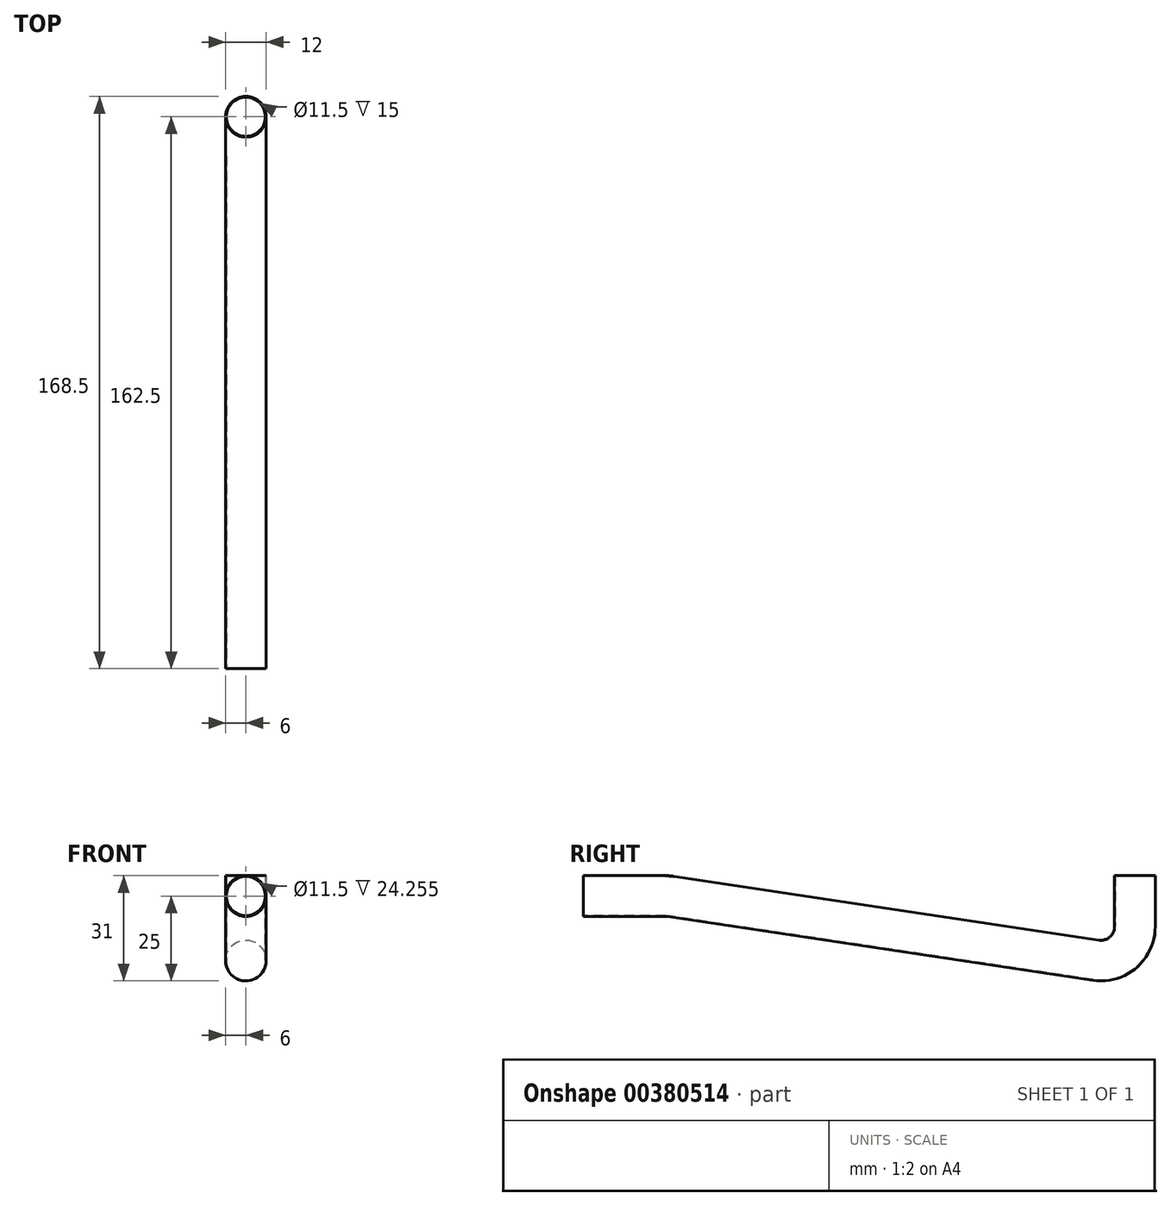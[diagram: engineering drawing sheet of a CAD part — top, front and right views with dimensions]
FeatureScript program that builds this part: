
annotation { "Feature Type Name" : "Feature", "Feature Type Description" : "" }
export const myFeature = defineFeature(function(context is Context, id is Id, definition is map)
    precondition{}
    {
        {
            var Q0;
            Q0=qCreatedBy(makeId("Right.planeOp"),FACE);
            var sketch = newSketch(context, id + "F0", { "sketchPlane" : qUnion([Q0])});
            skLineSegment(sketch, "E0", {"start": v(-162.5, -6) * mm, "end": v(-138.25, -6) * mm});
            skLineSegment(sketch, "E1", {"start": v(-136.76, -6.11) * mm, "end": v(-11.48, -24.89) * mm});
            skPoint(sketch, "E2.visualSharp", {"position": v(-137.5, -6) * mm});
            skArc(sketch, "E2.filletArc", {"start": v(-136.76, -6.11) * mm, "mid": v(-137.5, -6.03) * mm, "end": v(-138.25, -6) * mm});
            skLineSegment(sketch, "E3", {"start": v(0, -15) * mm, "end": v(0, 0) * mm});
            skPoint(sketch, "E4.visualSharp", {"position": v(0, 0) * mm});
            skArc(sketch, "E4.filletArc", {"start": v(-11.48, -24.89) * mm, "mid": v(-3.47, -22.58) * mm, "end": v(0, -15) * mm});
            skLineSegment(sketch, "E5", {"start": v(0, 0) * mm, "end": v(-6, 0) * mm});
            skLineSegment(sketch, "E6", {"start": v(-162.5, 0) * mm, "end": v(-162.5, -12) * mm});
            skLineSegment(sketch, "E7", {"start": v(-162.5, 0) * mm, "end": v(-137.5, 0) * mm});
            skLineSegment(sketch, "E8", {"start": v(-162.5, -12) * mm, "end": v(-138.25, -12) * mm});
            skLineSegment(sketch, "E9", {"start": v(-136.76, -12.11) * mm, "end": v(-7.78, -31.44) * mm});
            skLineSegment(sketch, "E10", {"start": v(-137.5, 0) * mm, "end": v(-15.19, -18.33) * mm});
            skLineSegment(sketch, "E11", {"start": v(-6, -10.42) * mm, "end": v(-6, 0) * mm});
            skLineSegment(sketch, "E12", {"start": v(6, -19.58) * mm, "end": v(6, 0) * mm});
            skLineSegment(sketch, "E13", {"start": v(6, 0) * mm, "end": v(-6, 0) * mm});
            skPoint(sketch, "E14.visualSharp", {"position": v(-6, -19.71) * mm});
            skArc(sketch, "E14.filletArc", {"start": v(-15.19, -18.33) * mm, "mid": v(-8.78, -16.48) * mm, "end": v(-6, -10.42) * mm});
            skPoint(sketch, "E15.visualSharp", {"position": v(6, -33.51) * mm});
            skArc(sketch, "E15.filletArc", {"start": v(-7.78, -31.44) * mm, "mid": v(1.83, -28.67) * mm, "end": v(6, -19.58) * mm});
            skPoint(sketch, "E16.visualSharp", {"position": v(-137.5, -12) * mm});
            skArc(sketch, "E16.filletArc", {"start": v(-136.76, -12.11) * mm, "mid": v(-137.5, -12.03) * mm, "end": v(-138.25, -12) * mm});
            skLineSegment(sketch, "E17", {"start": v(0, -15) * mm, "end": v(-187.69, -15) * mm, "construction": true});
            skLineSegment(sketch, "E18", {"start": v(-7.78, -31.44) * mm, "end": v(-162.5, -31.44) * mm, "construction": true});
            skLineSegment(sketch, "E19", {"start": v(-15.19, -18.33) * mm, "end": v(-162.5, -18.33) * mm, "construction": true});
            skLineSegment(sketch, "E20", {"start": v(-162.5, -31.44) * mm, "end": v(-162.5, -18.33) * mm, "construction": true});
            skLineSegment(sketch, "E21", {"start": v(-11.48, -24.89) * mm, "end": v(-162.5, -24.89) * mm, "construction": true});
            skSolve(sketch);
        }
        {
            var Q0;
            Q0=qCreatedBy(makeId("Top.planeOp"),FACE);
            var sketch = newSketch(context, id + "F1", { "sketchPlane" : qUnion([Q0])});
            skCircle(sketch, "E22", {"center": v(0, 0) * mm, "radius": 6 * mm});
            skCircle(sketch, "E23", {"center": v(0, 0) * mm, "radius": 5.75 * mm});
            skSolve(sketch);
        }
        {
            var Q0;
            Q0=makeQuery(id+"F1.imprint","IMPRINT",FACE,{"disambiguationData":[TD([[makeQuery(id+"F1.imprint","IMPRINT",EDGE,{"derivedFrom":sQuery(id+"F1.wireOp",EDGE,"E22")}),1.0]])]});
            var Q1;
            Q1=sQuery(id+"F0.wireOp",EDGE,"E3");
            var Q2;
            Q2=sQuery(id+"F0.wireOp",EDGE,"E4.filletArc");
            var Q3;
            Q3=sQuery(id+"F0.wireOp",EDGE,"E1");
            var Q4;
            Q4=sQuery(id+"F0.wireOp",EDGE,"E0");
            var Q5;
            Q5=sQuery(id+"F0.wireOp",EDGE,"E2.filletArc");
            sweep(context, id + "F2", {"profiles" : qUnion([Q0]), "path" : qUnion([Q1, Q2, Q3, Q4, Q5])});
        }
    });
